# Revit family: Kerberos TPB-S03
name_source: partatom
category: Türen
revit_build: Autodesk Revit 2016 (Build: 20150220_1215(x64)
units: mm (PartAtom-declared; Revit-internal decimal feet)

## family parameters
Arbeitsebenenbasiert = Nein
Beim Laden mit Abzugskörper schneiden = Nein
Gemeinsam genutzt = Nein
Immer vertikal = Ja
Raumberechnungspunkt = Nein

## types (1)
- TSB-S03
    Analytische Konstruktion = <Keine Auswahl>
    BarrierHeight = 900 mm  [stored 2.95276 ft]
    Breite = 555 mm  [stored 1.82087 ft]
    Design country = Germany
    Edition number = 1
    Funktion = Innen
    HasButtonEntrance = Nein
    HasButtonExit = Nein
    Hersteller = Dorma Kaba
    Höhe = 1100 mm  [stored 3.60892 ft]
    Konstruktionstyp = Access Barrier
    Length = 420 mm  [stored 1.37795 ft]
    Manufacturer country = Germany
    Manufacturer name = DORMA
    Material main = Metal
    Modell = TSB-S03
    Nominal height = 1100
    Nominal width = 810
    Product SKU = kerberos_TPB-S03
    Technical description = http://www.kaba.com
    URL = http://www.kaba.com

note: [stored X ft] marks values corroborated as IEEE doubles in the binary element streams (Revit-internal decimal feet)
